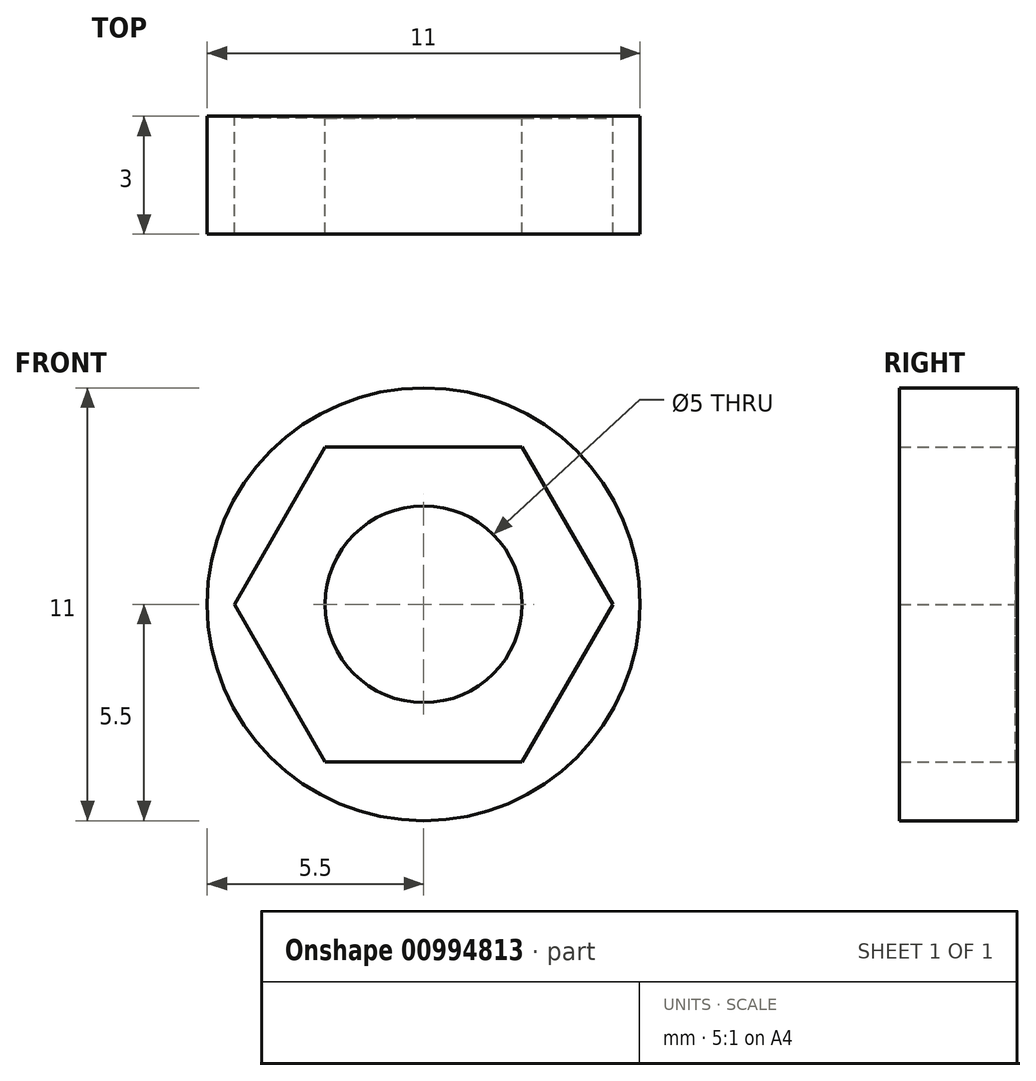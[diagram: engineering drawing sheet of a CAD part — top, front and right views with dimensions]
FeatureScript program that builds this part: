
annotation { "Feature Type Name" : "Feature", "Feature Type Description" : "" }
export const myFeature = defineFeature(function(context is Context, id is Id, definition is map)
    precondition{}
    {
        {
            var Q0;
            Q0=qCreatedBy(makeId("Front.planeOp"),FACE);
            var sketch = newSketch(context, id + "F0", { "sketchPlane" : qUnion([Q0])});
            skCircle(sketch, "E0", {"center": v(0, 0) * mm, "radius": 5.5 * mm});
            skLineSegment(sketch, "E1.bottom", {"start": v(-2.5, -4) * mm, "end": v(2.5, -4) * mm});
            skLineSegment(sketch, "E1.top", {"start": v(-2.5, 4) * mm, "end": v(2.5, 4) * mm});
            skLineSegment(sketch, "E1.left", {"start": v(-2.5, -4) * mm, "end": v(-2.5, 4) * mm});
            skLineSegment(sketch, "E1.right", {"start": v(2.5, -4) * mm, "end": v(2.5, 4) * mm});
            skLineSegment(sketch, "E2", {"start": v(-2.5, -4) * mm, "end": v(-4.8, 0) * mm});
            skLineSegment(sketch, "E3", {"start": v(-2.5, 4) * mm, "end": v(-4.8, 0) * mm});
            skLineSegment(sketch, "E4", {"start": v(2.5, 4) * mm, "end": v(4.8, 0) * mm});
            skLineSegment(sketch, "E5", {"start": v(4.8, 0) * mm, "end": v(2.5, -4) * mm});
            skSolve(sketch);
        }
        {
            var Q0;
            Q0=qSketchRegion(id+"F0",true);
            extrude(context, id + "F1", {"entities" : qUnion([Q0]), "depth" : 3 * mm, "offsetDistance" : 25.4 * mm});
        }
        {
            var Q0;
            Q0=qCreatedBy(makeId("Front.planeOp"),FACE);
            var sketch = newSketch(context, id + "F2", { "sketchPlane" : qUnion([Q0])});
            skLineSegment(sketch, "E6.bottom", {"start": v(-3.38, -4.1) * mm, "end": v(3.38, -4.1) * mm});
            skLineSegment(sketch, "E6.top", {"start": v(-3.38, 4.1) * mm, "end": v(3.38, 4.1) * mm});
            skLineSegment(sketch, "E6.left", {"start": v(-3.38, -4.1) * mm, "end": v(-3.38, 4.1) * mm});
            skLineSegment(sketch, "E6.right", {"start": v(3.38, -4.1) * mm, "end": v(3.38, 4.1) * mm});
            skPoint(sketch, "E6.middle", {"position": v(0, 0) * mm});
            skLineSegment(sketch, "E7.bottom", {"start": v(-3.38, 2) * mm, "end": v(-4.51, 2) * mm});
            skLineSegment(sketch, "E7.top", {"start": v(-3.38, -1.86) * mm, "end": v(-4.51, -1.86) * mm});
            skLineSegment(sketch, "E7.left", {"start": v(-3.38, 2) * mm, "end": v(-3.38, -1.86) * mm});
            skLineSegment(sketch, "E7.right", {"start": v(-4.51, 2) * mm, "end": v(-4.51, -1.86) * mm});
            skLineSegment(sketch, "E8.bottom", {"start": v(-4.51, 0.87) * mm, "end": v(-5.1, 0.87) * mm});
            skLineSegment(sketch, "E8.top", {"start": v(-4.51, -0.87) * mm, "end": v(-5.1, -0.87) * mm});
            skLineSegment(sketch, "E8.left", {"start": v(-4.51, 0.87) * mm, "end": v(-4.51, -0.87) * mm});
            skLineSegment(sketch, "E8.right", {"start": v(-5.1, 0.87) * mm, "end": v(-5.1, -0.87) * mm});
            skLineSegment(sketch, "E9.bottom", {"start": v(3.38, 2.34) * mm, "end": v(4.44, 2.34) * mm});
            skLineSegment(sketch, "E9.top", {"start": v(3.38, -2.17) * mm, "end": v(4.44, -2.17) * mm});
            skLineSegment(sketch, "E9.left", {"start": v(3.38, 2.34) * mm, "end": v(3.38, -2.17) * mm});
            skLineSegment(sketch, "E9.right", {"start": v(4.44, 2.34) * mm, "end": v(4.44, -2.17) * mm});
            skLineSegment(sketch, "E10.bottom", {"start": v(4.44, 1.04) * mm, "end": v(5, 1.04) * mm});
            skLineSegment(sketch, "E10.top", {"start": v(4.44, -0.87) * mm, "end": v(5, -0.87) * mm});
            skLineSegment(sketch, "E10.left", {"start": v(4.44, 1.04) * mm, "end": v(4.44, -0.87) * mm});
            skLineSegment(sketch, "E10.right", {"start": v(5, 1.04) * mm, "end": v(5, -0.87) * mm});
            skCircle(sketch, "E11", {"center": v(0, 0) * mm, "radius": 2.5 * mm});
            skLineSegment(sketch, "E12.bottom", {"start": v(-3.38, -1.86) * mm, "end": v(-4.14, -1.86) * mm});
            skLineSegment(sketch, "E12.top", {"start": v(-3.38, -2.57) * mm, "end": v(-4.14, -2.57) * mm});
            skLineSegment(sketch, "E12.left", {"start": v(-3.38, -1.86) * mm, "end": v(-3.38, -2.57) * mm});
            skLineSegment(sketch, "E12.right", {"start": v(-4.14, -1.86) * mm, "end": v(-4.14, -2.57) * mm});
            skPoint(sketch, "E13.oppositeSnap0", {"position": v(3.91, -2.17) * mm});
            skLineSegment(sketch, "E13.bottom", {"start": v(3.38, -2.17) * mm, "end": v(3.91, -2.17) * mm});
            skLineSegment(sketch, "E13.top", {"start": v(3.38, -2.75) * mm, "end": v(3.91, -2.75) * mm});
            skLineSegment(sketch, "E13.left", {"start": v(3.38, -2.17) * mm, "end": v(3.38, -2.75) * mm});
            skLineSegment(sketch, "E13.right", {"start": v(3.91, -2.17) * mm, "end": v(3.91, -2.75) * mm});
            skLineSegment(sketch, "E14.bottom", {"start": v(3.38, 2.34) * mm, "end": v(3.78, 2.34) * mm});
            skLineSegment(sketch, "E14.top", {"start": v(3.38, 2.9) * mm, "end": v(3.78, 2.9) * mm});
            skLineSegment(sketch, "E14.left", {"start": v(3.38, 2.34) * mm, "end": v(3.38, 2.9) * mm});
            skLineSegment(sketch, "E14.right", {"start": v(3.78, 2.34) * mm, "end": v(3.78, 2.9) * mm});
            skLineSegment(sketch, "E15.bottom", {"start": v(-3.38, 2) * mm, "end": v(-4.03, 2) * mm});
            skLineSegment(sketch, "E15.top", {"start": v(-3.38, 2.71) * mm, "end": v(-4.03, 2.71) * mm});
            skLineSegment(sketch, "E15.left", {"start": v(-3.38, 2) * mm, "end": v(-3.38, 2.71) * mm});
            skLineSegment(sketch, "E15.right", {"start": v(-4.03, 2) * mm, "end": v(-4.03, 2.71) * mm});
            skSolve(sketch);
        }
        {
            var Q0;
            Q0=qSketchRegion(id+"F2",true);
            extrude(context, id + "F3", {"entities" : qUnion([Q0]), "operationType" : NewBodyOperationType.ADD, "depth" : 0.05 * mm, "offsetDistance" : 25.4 * mm});
        }
    });
